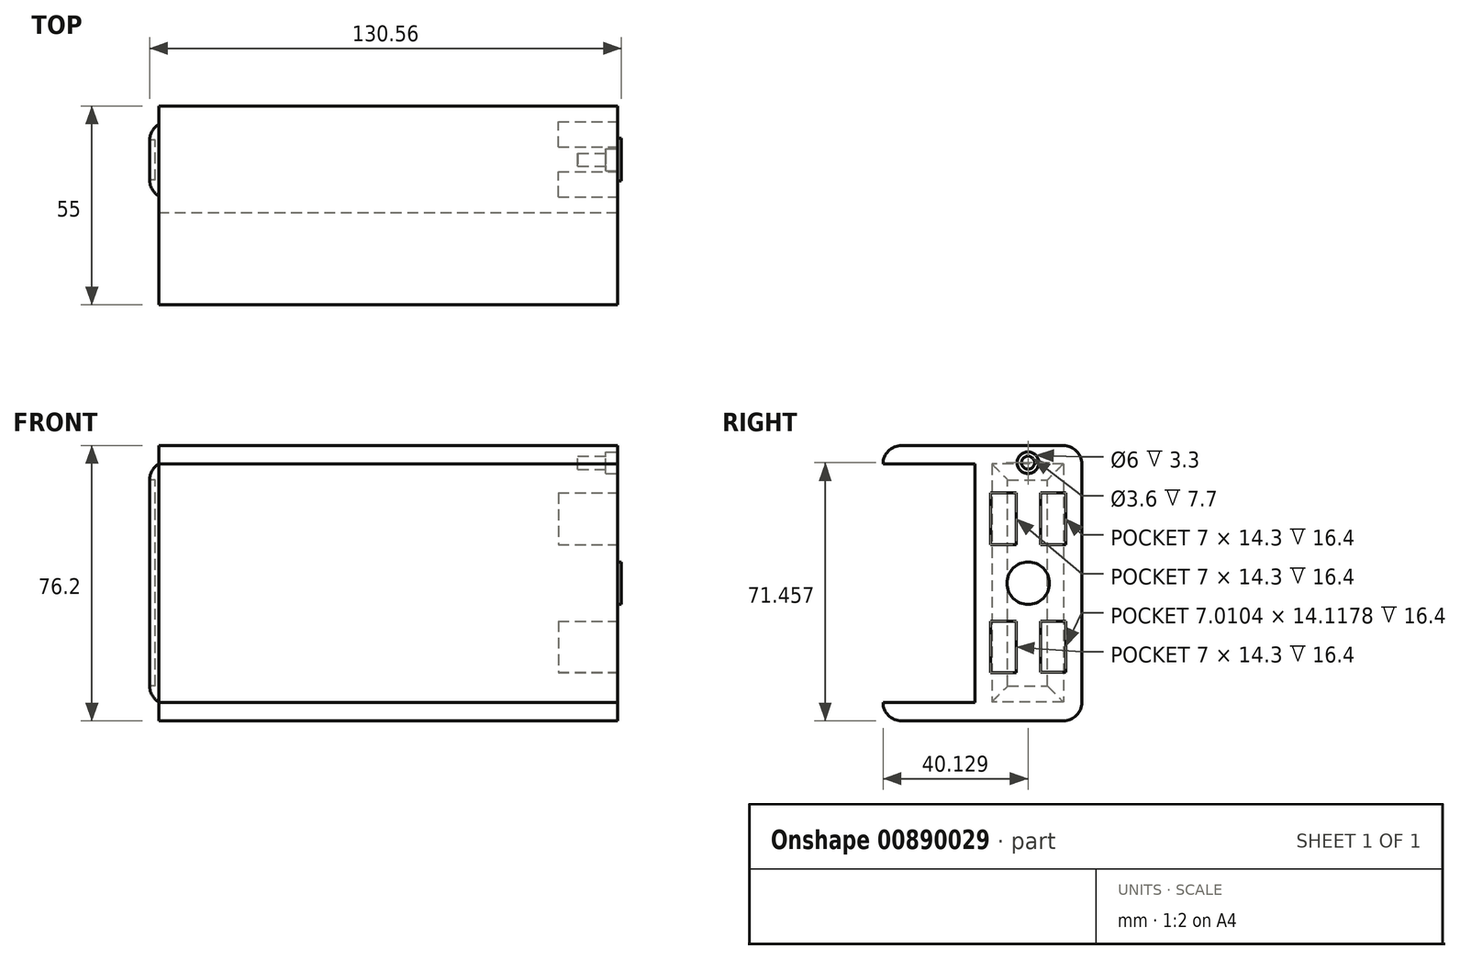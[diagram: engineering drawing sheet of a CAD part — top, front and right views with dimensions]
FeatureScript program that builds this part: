
annotation { "Feature Type Name" : "Feature", "Feature Type Description" : "" }
export const myFeature = defineFeature(function(context is Context, id is Id, definition is map)
    precondition{}
    {
        {
            var Q0;
            Q0=qCreatedBy(makeId("Front.planeOp"),FACE);
            var sketch = newSketch(context, id + "F0", { "sketchPlane" : qUnion([Q0])});
            skLineSegment(sketch, "E0.bottom", {"start": v(63.5, -38.1) * mm, "end": v(-63.5, -38.1) * mm});
            skLineSegment(sketch, "E0.top", {"start": v(63.5, 38.1) * mm, "end": v(-63.5, 38.1) * mm});
            skLineSegment(sketch, "E0.left", {"start": v(63.5, -38.1) * mm, "end": v(63.5, 38.1) * mm});
            skLineSegment(sketch, "E0.right", {"start": v(-63.5, -38.1) * mm, "end": v(-63.5, 38.1) * mm});
            skPoint(sketch, "E0.middle", {"position": v(0, 0) * mm});
            skSolve(sketch);
        }
        {
            var Q0;
            Q0=makeQuery(id+"F0.imprint","IMPRINT",FACE,{"disambiguationData":[TD([[makeQuery(id+"F0.imprint","IMPRINT",EDGE,{"derivedFrom":sQuery(id+"F0.wireOp",EDGE,"E0.bottom")}),-1.0]])]});
            extrude(context, id + "F1", {"entities" : qUnion([Q0]), "depth" : 55 * mm, "offsetDistance" : 25.4 * mm});
        }
        {
            var Q0;
            Q0=makeQuery(id+"F1.opExtrude","CAP_EDGE",EDGE,{"disambiguationData":[OSD([sQuery(id+"F0.wireOp",EDGE,"E0.bottom")])],"isStart":false});
            var Q1;
            Q1=makeQuery(id+"F1.opExtrude","CAP_EDGE",EDGE,{"disambiguationData":[OSD([sQuery(id+"F0.wireOp",EDGE,"E0.bottom")])],"isStart":true});
            var Q2;
            Q2=makeQuery(id+"F1.opExtrude","CAP_EDGE",EDGE,{"disambiguationData":[OSD([sQuery(id+"F0.wireOp",EDGE,"E0.top")])],"isStart":false});
            var Q3;
            Q3=makeQuery(id+"F1.opExtrude","CAP_EDGE",EDGE,{"disambiguationData":[OSD([sQuery(id+"F0.wireOp",EDGE,"E0.top")])],"isStart":true});
            fillet(context, id + "F2", {"entities" : qUnion([Q0, Q1, Q2, Q3]), "radius" : 5.08 * mm, "tangentPropagation" : true, "allowEdgeOverflow" : false});
        }
        {
            var Q0;
            Q0=makeQuery(id+"F1.opExtrude","SWEPT_FACE",FACE,{"disambiguationData":[OSD([sQuery(id+"F0.wireOp",EDGE,"E0.left")])]});
            var sketch = newSketch(context, id + "F3", { "sketchPlane" : qUnion([Q0])});
            skLineSegment(sketch, "E1", {"start": v(-55, 25.02) * mm, "end": v(-55, 10.72) * mm});
            skLineSegment(sketch, "E2", {"start": v(0, 25.02) * mm, "end": v(0, 10.72) * mm});
            skLineSegment(sketch, "E3.bottom", {"start": v(-52.81, 25.02) * mm, "end": v(-45.81, 25.02) * mm});
            skLineSegment(sketch, "E3.top", {"start": v(-52.81, 10.72) * mm, "end": v(-45.81, 10.72) * mm});
            skLineSegment(sketch, "E3.left", {"start": v(-52.81, 25.02) * mm, "end": v(-52.81, 10.72) * mm});
            skLineSegment(sketch, "E3.right", {"start": v(-45.81, 25.02) * mm, "end": v(-45.81, 10.72) * mm});
            skLineSegment(sketch, "E4.bottom", {"start": v(-38.7, 25.02) * mm, "end": v(-31.7, 25.02) * mm});
            skLineSegment(sketch, "E4.top", {"start": v(-38.7, 10.72) * mm, "end": v(-31.7, 10.72) * mm});
            skLineSegment(sketch, "E4.left", {"start": v(-38.7, 25.02) * mm, "end": v(-38.7, 10.72) * mm});
            skLineSegment(sketch, "E4.right", {"start": v(-31.7, 25.02) * mm, "end": v(-31.7, 10.72) * mm});
            skLineSegment(sketch, "E5.bottom", {"start": v(-25.18, 25.02) * mm, "end": v(-18.18, 25.02) * mm});
            skLineSegment(sketch, "E5.top", {"start": v(-25.18, 10.72) * mm, "end": v(-18.18, 10.72) * mm});
            skLineSegment(sketch, "E5.left", {"start": v(-25.18, 25.02) * mm, "end": v(-25.18, 10.72) * mm});
            skLineSegment(sketch, "E5.right", {"start": v(-18.18, 25.02) * mm, "end": v(-18.18, 10.72) * mm});
            skLineSegment(sketch, "E6.bottom", {"start": v(-11.37, 25.02) * mm, "end": v(-4.37, 25.02) * mm});
            skLineSegment(sketch, "E6.top", {"start": v(-11.37, 10.72) * mm, "end": v(-4.37, 10.72) * mm});
            skLineSegment(sketch, "E6.left", {"start": v(-11.37, 25.02) * mm, "end": v(-11.37, 10.72) * mm});
            skLineSegment(sketch, "E6.right", {"start": v(-4.37, 25.02) * mm, "end": v(-4.37, 10.72) * mm});
            skSolve(sketch);
        }
        {
            var Q0;
            Q0=makeQuery(id+"F3.imprint","IMPRINT",FACE,{"disambiguationData":[TD([[makeQuery(id+"F3.imprint","IMPRINT",EDGE,{"derivedFrom":sQuery(id+"F3.wireOp",EDGE,"E3.bottom")}),-1.0]])]});
            var Q1;
            Q1=makeQuery(id+"F3.imprint","IMPRINT",FACE,{"disambiguationData":[TD([[makeQuery(id+"F3.imprint","IMPRINT",EDGE,{"derivedFrom":sQuery(id+"F3.wireOp",EDGE,"E4.bottom")}),-1.0]])]});
            var Q2;
            Q2=makeQuery(id+"F3.imprint","IMPRINT",FACE,{"disambiguationData":[TD([[makeQuery(id+"F3.imprint","IMPRINT",EDGE,{"derivedFrom":sQuery(id+"F3.wireOp",EDGE,"E5.bottom")}),-1.0]])]});
            var Q3;
            Q3=makeQuery(id+"F3.imprint","IMPRINT",FACE,{"disambiguationData":[TD([[makeQuery(id+"F3.imprint","IMPRINT",EDGE,{"derivedFrom":sQuery(id+"F3.wireOp",EDGE,"E6.bottom")}),-1.0]])]});
            extrude(context, id + "F4", {"entities" : qUnion([Q0, Q1, Q2, Q3]), "operationType" : NewBodyOperationType.REMOVE, "oppositeDirection" : true, "depth" : 16.4 * mm, "offsetDistance" : 25.4 * mm});
        }
        {
            var Q0;
            Q0=makeQuery(id+"F1.opExtrude","CAP_FACE",FACE,{"disambiguationData":[OSD([sQuery(id+"F0.wireOp",EDGE,"E0.bottom"),sQuery(id+"F0.wireOp",EDGE,"E0.top"),sQuery(id+"F0.wireOp",EDGE,"E0.left"),sQuery(id+"F0.wireOp",EDGE,"E0.right")])],"isStart":false});
            extrude(context, id + "F5", {"entities" : qUnion([Q0]), "operationType" : NewBodyOperationType.REMOVE, "oppositeDirection" : true, "depth" : 25.4 * mm, "offsetDistance" : 25.4 * mm});
        }
        {
            var Q0;
            Q0=makeQuery(id+"F1.opExtrude","SWEPT_FACE",FACE,{"disambiguationData":[OSD([sQuery(id+"F0.wireOp",EDGE,"E0.left")])]});
            var sketch = newSketch(context, id + "F6", { "sketchPlane" : qUnion([Q0])});
            skLineSegment(sketch, "E7.bottom", {"start": v(-25.18, -10.49) * mm, "end": v(-18.18, -10.49) * mm});
            skLineSegment(sketch, "E7.top", {"start": v(-25.18, -24.79) * mm, "end": v(-18.18, -24.79) * mm});
            skLineSegment(sketch, "E7.left", {"start": v(-25.18, -10.49) * mm, "end": v(-25.18, -24.79) * mm});
            skLineSegment(sketch, "E7.right", {"start": v(-18.18, -10.49) * mm, "end": v(-18.18, -24.79) * mm});
            skLineSegment(sketch, "E8.bottom", {"start": v(-11.37, -10.49) * mm, "end": v(-4.36, -10.49) * mm});
            skLineSegment(sketch, "E8.top", {"start": v(-11.37, -24.6) * mm, "end": v(-4.36, -24.6) * mm});
            skLineSegment(sketch, "E8.left", {"start": v(-11.37, -10.49) * mm, "end": v(-11.37, -24.6) * mm});
            skLineSegment(sketch, "E8.right", {"start": v(-4.36, -10.49) * mm, "end": v(-4.36, -24.6) * mm});
            skSolve(sketch);
        }
        {
            var Q0;
            Q0=makeQuery(id+"F6.imprint","IMPRINT",FACE,{"disambiguationData":[TD([[makeQuery(id+"F6.imprint","IMPRINT",EDGE,{"derivedFrom":sQuery(id+"F6.wireOp",EDGE,"E7.bottom")}),-1.0]])]});
            var Q1;
            Q1=makeQuery(id+"F6.imprint","IMPRINT",FACE,{"disambiguationData":[TD([[makeQuery(id+"F6.imprint","IMPRINT",EDGE,{"derivedFrom":sQuery(id+"F6.wireOp",EDGE,"E8.bottom")}),-1.0]])]});
            extrude(context, id + "F7", {"entities" : qUnion([Q0, Q1]), "operationType" : NewBodyOperationType.REMOVE, "oppositeDirection" : true, "depth" : 16.4 * mm, "offsetDistance" : 25.4 * mm});
        }
        {
            var Q0;
            Q0=makeQuery(id+"F1.opExtrude","SWEPT_FACE",FACE,{"disambiguationData":[OSD([sQuery(id+"F0.wireOp",EDGE,"E0.left")])]});
            var sketch = newSketch(context, id + "F8", { "sketchPlane" : qUnion([Q0])});
            skCircle(sketch, "E9", {"center": v(-14.82, 0) * mm, "radius": 5.88 * mm});
            skSolve(sketch);
        }
        {
            var Q0;
            Q0=makeQuery(id+"F1.opExtrude","SWEPT_FACE",FACE,{"disambiguationData":[OSD([sQuery(id+"F0.wireOp",EDGE,"E0.right")])]});
            var sketch = newSketch(context, id + "F9", { "sketchPlane" : qUnion([Q0])});
            skLineSegment(sketch, "E10.bottom", {"start": v(5.08, 33.02) * mm, "end": v(24.9, 33.02) * mm});
            skLineSegment(sketch, "E10.top", {"start": v(5.08, -32.86) * mm, "end": v(24.9, -32.86) * mm});
            skLineSegment(sketch, "E10.left", {"start": v(5.08, 33.02) * mm, "end": v(5.08, -32.86) * mm});
            skLineSegment(sketch, "E10.right", {"start": v(24.9, 33.02) * mm, "end": v(24.9, -32.86) * mm});
            skSolve(sketch);
        }
        {
            var Q0;
            Q0=makeQuery(id+"F9.imprint","IMPRINT",FACE,{"disambiguationData":[TD([[makeQuery(id+"F9.imprint","IMPRINT",EDGE,{"derivedFrom":sQuery(id+"F9.wireOp",EDGE,"E10.bottom")}),-1.0]])]});
            extrude(context, id + "F10", {"entities" : qUnion([Q0]), "operationType" : NewBodyOperationType.ADD, "depth" : 2.54 * mm, "offsetDistance" : 25.4 * mm});
        }
        {
            var Q0;
            Q0=makeQuery(id+"F10.opExtrude","CAP_EDGE",EDGE,{"disambiguationData":[OSD([sQuery(id+"F9.wireOp",EDGE,"E10.right")])],"isStart":false});
            var Q1;
            Q1=makeQuery(id+"F10.opExtrude","CAP_EDGE",EDGE,{"disambiguationData":[OSD([sQuery(id+"F9.wireOp",EDGE,"E10.bottom")])],"isStart":false});
            var Q2;
            Q2=makeQuery(id+"F10.opExtrude","CAP_EDGE",EDGE,{"disambiguationData":[OSD([sQuery(id+"F9.wireOp",EDGE,"E10.top")])],"isStart":false});
            var Q3;
            Q3=makeQuery(id+"F10.opExtrude","CAP_EDGE",EDGE,{"disambiguationData":[OSD([sQuery(id+"F9.wireOp",EDGE,"E10.left")])],"isStart":false});
            fillet(context, id + "F11", {"entities" : qUnion([Q0, Q1, Q2, Q3]), "radius" : 5.08 * mm, "tangentPropagation" : true, "allowEdgeOverflow" : false});
        }
        {
            var Q0;
            Q0=makeQuery(id+"F10.opExtrude","CAP_FACE",FACE,{"disambiguationData":[OSD([sQuery(id+"F9.wireOp",EDGE,"E10.bottom"),sQuery(id+"F9.wireOp",EDGE,"E10.top"),sQuery(id+"F9.wireOp",EDGE,"E10.left"),sQuery(id+"F9.wireOp",EDGE,"E10.right")])],"isStart":false});
            extrude(context, id + "F12", {"entities" : qUnion([Q0]), "operationType" : NewBodyOperationType.REMOVE, "oppositeDirection" : true, "depth" : 1.52 * mm, "offsetDistance" : 25.4 * mm});
        }
        {
            var Q0;
            Q0=makeQuery(id+"F1.opExtrude","SWEPT_FACE",FACE,{"disambiguationData":[OSD([sQuery(id+"F0.wireOp",EDGE,"E0.left")])]});
            var sketch = newSketch(context, id + "F13", { "sketchPlane" : qUnion([Q0])});
            skCircle(sketch, "E11", {"center": v(-14.87, 33.36) * mm, "radius": 3 * mm});
            skCircle(sketch, "E12", {"center": v(-14.87, 33.36) * mm, "radius": 1.8 * mm});
            skSolve(sketch);
        }
        {
            var Q0;
            Q0=makeQuery(id+"F13.imprint","IMPRINT",FACE,{"disambiguationData":[TD([[makeQuery(id+"F13.imprint","IMPRINT",EDGE,{"derivedFrom":sQuery(id+"F13.wireOp",EDGE,"E11")}),1.0]])]});
            extrude(context, id + "F14", {"entities" : qUnion([Q0]), "operationType" : NewBodyOperationType.REMOVE, "oppositeDirection" : true, "depth" : 3.3 * mm, "offsetDistance" : 25.4 * mm});
        }
        {
            var Q0;
            Q0=makeQuery(id+"F14.boolean.opBoolean","SPLIT",FACE,{"disambiguationData":[TD([makeQuery(id+"F14.opExtrude","SWEPT_FACE",FACE,{"disambiguationData":[OSD([sQuery(id+"F13.wireOp",EDGE,"E12")])]})])],"derivedFrom":makeQuery(id+"F1.opExtrude","SWEPT_FACE",FACE,{"disambiguationData":[OSD([sQuery(id+"F0.wireOp",EDGE,"E0.left")])]})});
            extrude(context, id + "F15", {"entities" : qUnion([Q0]), "operationType" : NewBodyOperationType.REMOVE, "oppositeDirection" : true, "depth" : 11 * mm, "offsetDistance" : 25.4 * mm});
        }
        {
            var Q0;
            Q0=makeQuery(id+"F8.imprint","IMPRINT",FACE,{"disambiguationData":[TD([[makeQuery(id+"F8.imprint","IMPRINT",EDGE,{"derivedFrom":sQuery(id+"F8.wireOp",EDGE,"E9")}),1.0]])]});
            extrude(context, id + "F16", {"entities" : qUnion([Q0]), "operationType" : NewBodyOperationType.ADD, "depth" : 1.02 * mm, "offsetDistance" : 25.4 * mm});
        }
    });
